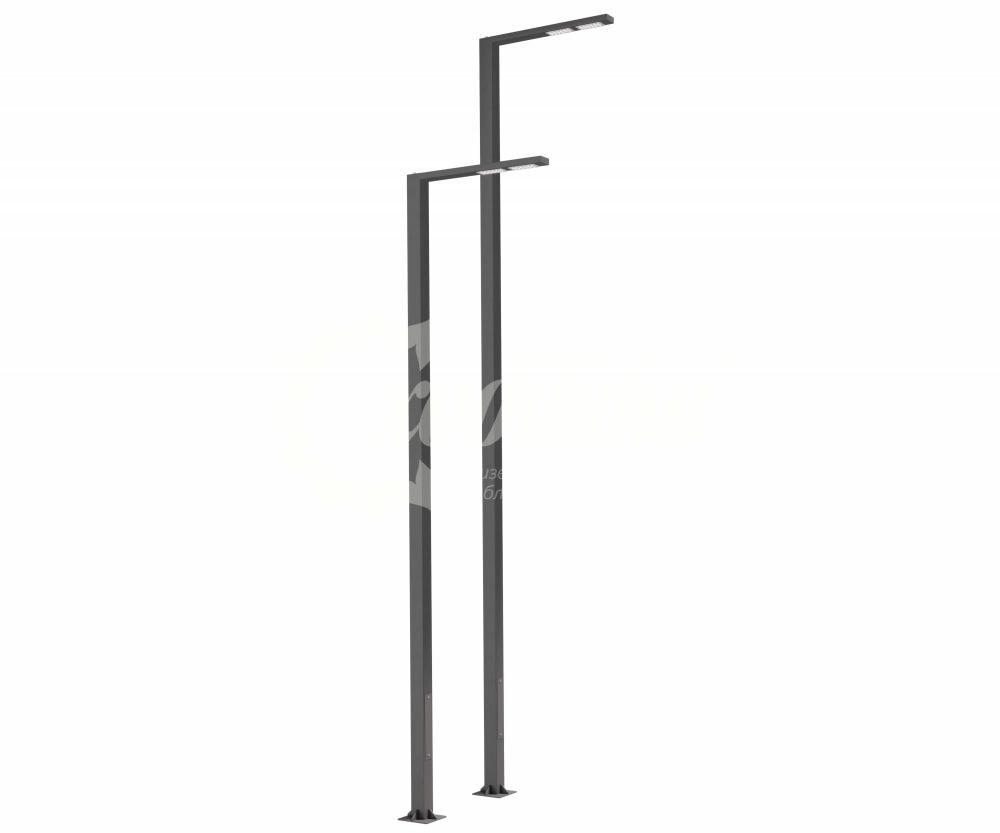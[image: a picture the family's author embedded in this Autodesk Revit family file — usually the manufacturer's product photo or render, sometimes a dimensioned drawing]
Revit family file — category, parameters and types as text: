
# Revit family: 23526 Стальной светодиодный столб «Иннополис» Хоббика
name_source: partatom
category: Антураж
revit_build: Autodesk Revit 2018 (Build: 20180423_1000(x64)
units: mm (PartAtom-declared; Revit-internal decimal feet)

## family parameters
Всегда вертикально = Да
Источник визуального образа = Геометрия семейства
На основе рабочей плоскости = Нет
Общий = Нет
При загрузке вырезать с полостями = Нет
Точка расчета площади = Нет

## types (2) — shared parameters
URL = https://hobbyka.ru
Артикул товара = Арт. 23526
Группа модели = Светильники со стальными опорами
Длина = 950 мм
Изготовитель = ООО «Хоббика»
Изображение типоразмера = Стальной светодиодный столб «Иннополис» Арт 23526.jpg
Материал изделия = Сталь
Цвет каркаса = Сталь
Ширина = 300 мм

## per-type parameters (varying)
| type | Версия 4,0 м | Версия 5,0 м | Высота | Описание |
| Версия 4,0 м | Да | Нет | 4000 мм | Стальной светодиодный столб «Иннополис». Версия 4,0 м (28 Вт) |
| Версия 5,0 м | Нет | Да | 5000 мм | Стальной светодиодный столб «Иннополис». Версия 5,0 м (28 Вт) |
